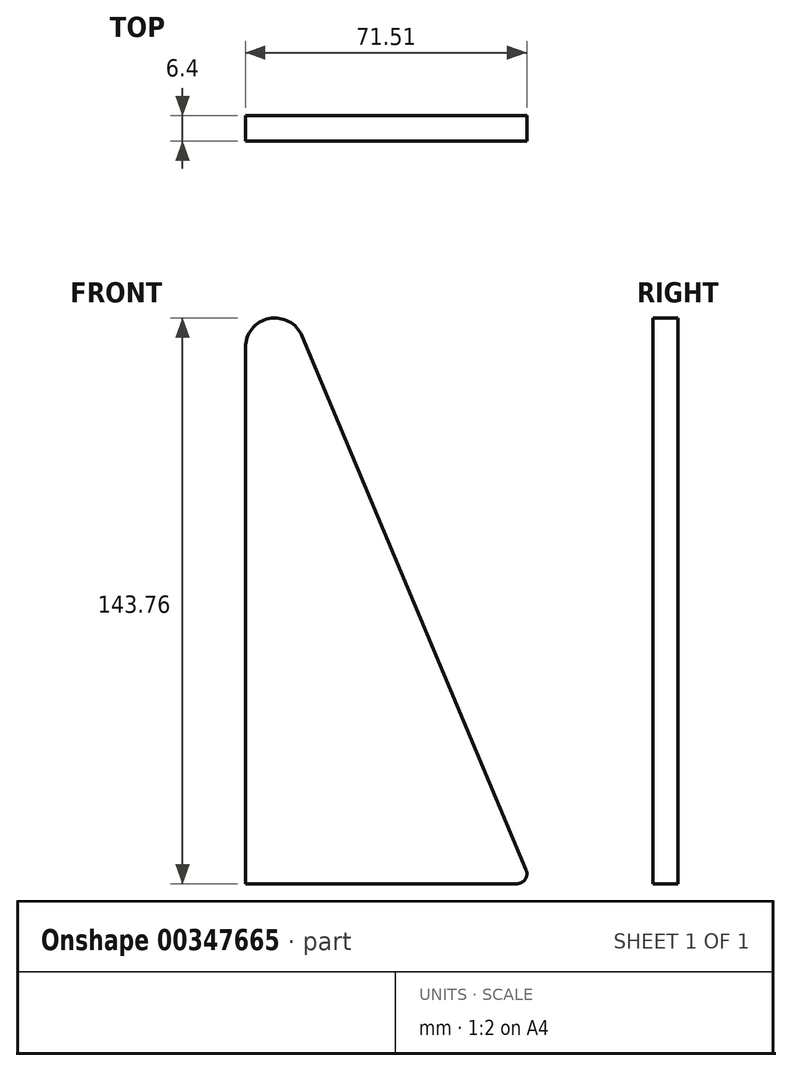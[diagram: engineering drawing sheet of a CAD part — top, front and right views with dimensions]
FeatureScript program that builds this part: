
annotation { "Feature Type Name" : "Feature", "Feature Type Description" : "" }
export const myFeature = defineFeature(function(context is Context, id is Id, definition is map)
    precondition{}
    {
        {
            var Q0;
            Q0=qCreatedBy(makeId("Front.planeOp"),FACE);
            var sketch = newSketch(context, id + "F0", { "sketchPlane" : qUnion([Q0])});
            skLineSegment(sketch, "E0", {"start": v(-16.5, -142.43) * mm, "end": v(52.44, -142.43) * mm});
            skLineSegment(sketch, "E1", {"start": v(-16.5, -142.43) * mm, "end": v(-16.5, -6.17) * mm});
            skLineSegment(sketch, "E2", {"start": v(-2.09, -3.27) * mm, "end": v(54.8, -138.87) * mm});
            skPoint(sketch, "E3.visualSharp", {"position": v(-16.5, 31.08) * mm});
            skArc(sketch, "E3.filletArc", {"start": v(-2.09, -3.27) * mm, "mid": v(-10.48, 1.18) * mm, "end": v(-16.5, -6.17) * mm});
            skPoint(sketch, "E4.visualSharp", {"position": v(56.3, -142.43) * mm});
            skArc(sketch, "E4.filletArc", {"start": v(52.44, -142.43) * mm, "mid": v(54.58, -141.28) * mm, "end": v(54.8, -138.87) * mm});
            skSolve(sketch);
        }
        {
            var Q0;
            Q0 = qSketchRegion(id + "F0", true);
            extrude(context, id + "F1", {"entities" : qUnion([Q0]), "oppositeDirection" : true, "depth" : 6.4 * mm});
        }
    });
